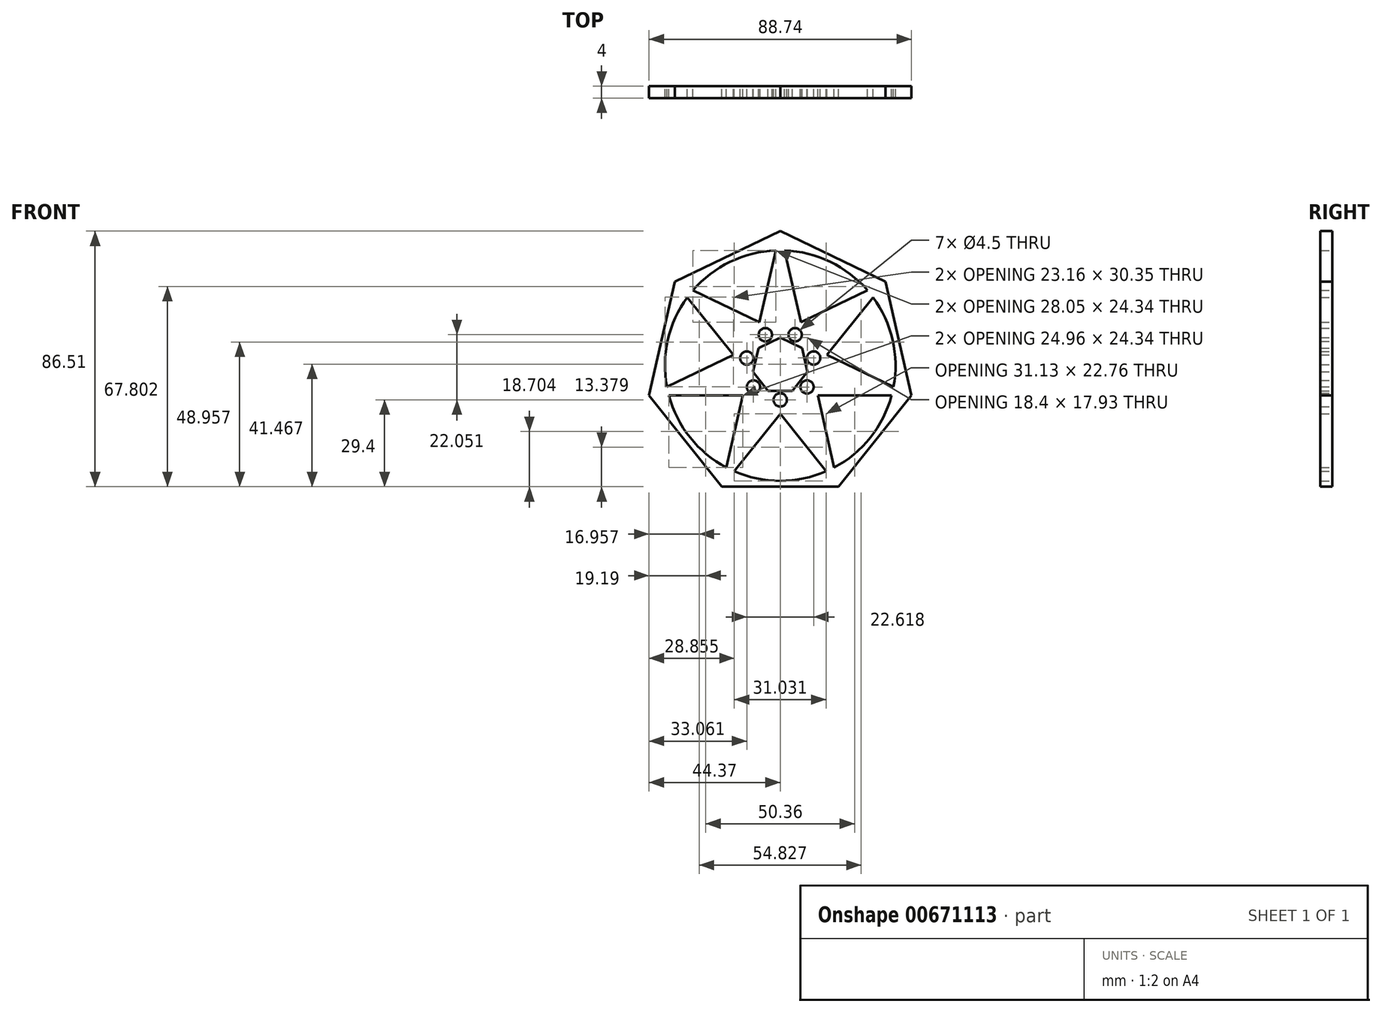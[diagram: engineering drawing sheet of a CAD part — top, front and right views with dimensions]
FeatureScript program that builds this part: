
annotation { "Feature Type Name" : "Feature", "Feature Type Description" : "" }
export const myFeature = defineFeature(function(context is Context, id is Id, definition is map)
    precondition{}
    {
        {
            var Q0;
            Q0=qCreatedBy(makeId("Front.planeOp"),FACE);
            var sketch = newSketch(context, id + "F0", { "sketchPlane" : qUnion([Q0])});
            skEllipse(sketch, "E0", {"center": v(0, 0) * mm, "majorRadius": 60 * mm, "minorRadius": 47.5 * mm, "majorAxis": v(-1, 0)});
            skLineSegment(sketch, "E1", {"start": v(-35.58, 28.37) * mm, "end": v(0, 11.24) * mm});
            skLineSegment(sketch, "E2", {"start": v(-35.58, 28.37) * mm, "end": v(-10.96, -2.5) * mm});
            skLineSegment(sketch, "E3", {"start": v(19.74, -41) * mm, "end": v(10.96, -2.5) * mm});
            skLineSegment(sketch, "E4", {"start": v(-19.74, -41) * mm, "end": v(4.88, -10.13) * mm});
            skLineSegment(sketch, "E5", {"start": v(-44.37, -10.13) * mm, "end": v(-4.88, -10.13) * mm});
            skLineSegment(sketch, "E6", {"start": v(0, 45.5) * mm, "end": v(-8.79, 7) * mm});
            skLineSegment(sketch, "E7", {"start": v(35.58, 28.37) * mm, "end": v(0, 11.24) * mm});
            skCircle(sketch, "E8.cCircle", {"center": v(0, 0) * mm, "radius": 8.5 * mm, "construction": true});
            skLineSegment(sketch, "E8.0", {"start": v(-7.38, 5.88) * mm, "end": v(0, 9.43) * mm});
            skLineSegment(sketch, "E8.1", {"start": v(0, 9.43) * mm, "end": v(7.38, 5.88) * mm});
            skLineSegment(sketch, "E8.2", {"start": v(7.38, 5.88) * mm, "end": v(9.2, -2.1) * mm});
            skLineSegment(sketch, "E8.3", {"start": v(9.2, -2.1) * mm, "end": v(4.1, -8.5) * mm});
            skLineSegment(sketch, "E8.4", {"start": v(4.1, -8.5) * mm, "end": v(-4.1, -8.5) * mm});
            skLineSegment(sketch, "E8.5", {"start": v(-4.1, -8.5) * mm, "end": v(-9.2, -2.1) * mm});
            skLineSegment(sketch, "E8.6", {"start": v(-9.2, -2.1) * mm, "end": v(-7.38, 5.88) * mm});
            skPoint(sketch, "E8.0.midPoint", {"position": v(-3.69, 7.66) * mm});
            skLineSegment(sketch, "E9.trimOffspring", {"start": v(-8.79, 7) * mm, "end": v(-44.37, -10.13) * mm});
            skLineSegment(sketch, "E10.trimOffspring", {"start": v(8.79, 7) * mm, "end": v(44.37, -10.13) * mm});
            skLineSegment(sketch, "E11.trimOffspring", {"start": v(8.79, 7) * mm, "end": v(0, 45.5) * mm});
            skLineSegment(sketch, "E12.trimOffspring", {"start": v(10.96, -2.5) * mm, "end": v(35.58, 28.37) * mm});
            skLineSegment(sketch, "E13.trimOffspring", {"start": v(4.88, -10.13) * mm, "end": v(44.37, -10.13) * mm});
            skLineSegment(sketch, "E14.trimOffspring", {"start": v(-4.88, -10.13) * mm, "end": v(19.74, -41) * mm});
            skLineSegment(sketch, "E15.trimOffspring", {"start": v(-10.96, -2.5) * mm, "end": v(-19.74, -41) * mm});
            skLineSegment(sketch, "E16", {"start": v(-15.83, 3.61) * mm, "end": v(0, 0) * mm, "construction": true});
            skCircle(sketch, "E17", {"center": v(-11.3, 2.58) * mm, "radius": 2.25 * mm});
            skCircle(sketch, "E18.1.0", {"center": v(-9.07, -7.23) * mm, "radius": 2.25 * mm});
            skCircle(sketch, "E18.2.0", {"center": v(0, -11.6) * mm, "radius": 2.25 * mm});
            skCircle(sketch, "E19.1.3.0", {"center": v(9.07, -7.23) * mm, "radius": 2.25 * mm});
            skCircle(sketch, "E19.1.4.0", {"center": v(11.3, 2.58) * mm, "radius": 2.25 * mm});
            skCircle(sketch, "E19.1.5.0", {"center": v(5.03, 10.45) * mm, "radius": 2.25 * mm});
            skCircle(sketch, "E19.1.6.0", {"center": v(-5.03, 10.45) * mm, "radius": 2.25 * mm});
            skCircle(sketch, "E20", {"center": v(0, 0) * mm, "radius": 39 * mm});
            skCircle(sketch, "E21.cCircle", {"center": v(0, 0) * mm, "radius": 41 * mm, "construction": true});
            skLineSegment(sketch, "E21.0", {"start": v(-35.58, 28.37) * mm, "end": v(0, 45.5) * mm});
            skLineSegment(sketch, "E21.1", {"start": v(0, 45.5) * mm, "end": v(35.58, 28.37) * mm});
            skLineSegment(sketch, "E21.2", {"start": v(35.58, 28.37) * mm, "end": v(44.37, -10.13) * mm});
            skLineSegment(sketch, "E21.3", {"start": v(44.37, -10.13) * mm, "end": v(19.74, -41) * mm});
            skLineSegment(sketch, "E21.4", {"start": v(19.74, -41) * mm, "end": v(-19.74, -41) * mm});
            skLineSegment(sketch, "E21.5", {"start": v(-19.74, -41) * mm, "end": v(-44.37, -10.13) * mm});
            skLineSegment(sketch, "E21.6", {"start": v(-44.37, -10.13) * mm, "end": v(-35.58, 28.37) * mm});
            skPoint(sketch, "E21.0.midPoint", {"position": v(-17.79, 36.94) * mm});
            skSolve(sketch);
        }
        {
            var Q0;
            {var subQ5=sQuery(id+"F0.wireOp",EDGE,"E1");var subQ7=sQuery(id+"F0.wireOp",EDGE,"E20");var subQ9=makeQuery(id+"F0.imprint","INTERSECT",VERTEX,{"derivedFrom":[subQ5,subQ7]});Q0=makeQuery(id+"F0.imprint","IMPRINT",FACE,{"disambiguationData":[TD([[makeQuery(id+"F0.imprint","IMPRINT",EDGE,{"disambiguationData":[TD([[subQ9,-1.0]])],"derivedFrom":subQ5}),-1.0]])]});}
            var Q1;
            {var subQ1=sQuery(id+"F0.wireOp",EDGE,"E7");var subQ5=sQuery(id+"F0.wireOp",EDGE,"E1");var subQ6=makeQuery(id+"F0.imprint","INTERSECT",VERTEX,{"derivedFrom":[subQ5,subQ1]});Q1=makeQuery(id+"F0.imprint","IMPRINT",FACE,{"disambiguationData":[TD([[makeQuery(id+"F0.imprint","IMPRINT",EDGE,{"disambiguationData":[TD([[subQ6,1.0]])],"derivedFrom":subQ5}),1.0]])]});}
            var Q2;
            Q2=makeQuery(id+"F0.imprint","IMPRINT",FACE,{"disambiguationData":[TD([[makeQuery(id+"F0.imprint","IMPRINT",EDGE,{"derivedFrom":sQuery(id+"F0.wireOp",EDGE,"E8.0")}),1.0]])]});
            var Q3;
            {var subQ3=sQuery(id+"F0.wireOp",EDGE,"E20");var subQ7=sQuery(id+"F0.wireOp",EDGE,"E7");var subQ9=makeQuery(id+"F0.imprint","INTERSECT",VERTEX,{"derivedFrom":[subQ7,subQ3]});Q3=makeQuery(id+"F0.imprint","IMPRINT",FACE,{"disambiguationData":[TD([[makeQuery(id+"F0.imprint","IMPRINT",EDGE,{"disambiguationData":[TD([[subQ9,-1.0]])],"derivedFrom":subQ7}),1.0]])]});}
            var Q4;
            {var subQ1=sQuery(id+"F0.wireOp",EDGE,"E3");var subQ5=sQuery(id+"F0.wireOp",EDGE,"E12.trimOffspring");var subQ6=makeQuery(id+"F0.imprint","INTERSECT",VERTEX,{"derivedFrom":[subQ1,subQ5]});Q4=makeQuery(id+"F0.imprint","IMPRINT",FACE,{"disambiguationData":[TD([[makeQuery(id+"F0.imprint","IMPRINT",EDGE,{"disambiguationData":[TD([[subQ6,1.0]])],"derivedFrom":subQ1}),-1.0]])]});}
            var Q5;
            {var subQ3=sQuery(id+"F0.wireOp",EDGE,"E20");var subQ7=sQuery(id+"F0.wireOp",EDGE,"E3");var subQ8=makeQuery(id+"F0.imprint","INTERSECT",VERTEX,{"derivedFrom":[subQ7,subQ3]});Q5=makeQuery(id+"F0.imprint","IMPRINT",FACE,{"disambiguationData":[TD([[makeQuery(id+"F0.imprint","IMPRINT",EDGE,{"disambiguationData":[TD([[subQ8,-1.0]])],"derivedFrom":subQ7}),1.0]])]});}
            var Q6;
            {var subQ3=sQuery(id+"F0.wireOp",EDGE,"E20");var subQ7=sQuery(id+"F0.wireOp",EDGE,"E4");var subQ9=makeQuery(id+"F0.imprint","INTERSECT",VERTEX,{"derivedFrom":[subQ7,subQ3]});Q6=makeQuery(id+"F0.imprint","IMPRINT",FACE,{"disambiguationData":[TD([[makeQuery(id+"F0.imprint","IMPRINT",EDGE,{"disambiguationData":[TD([[subQ9,-1.0]])],"derivedFrom":subQ7}),1.0]])]});}
            var Q7;
            {var subQ0=sQuery(id+"F0.wireOp",EDGE,"E15.trimOffspring");var subQ1=sQuery(id+"F0.wireOp",EDGE,"E2");var subQ2=makeQuery(id+"F0.imprint","INTERSECT",VERTEX,{"derivedFrom":[subQ1,subQ0]});Q7=makeQuery(id+"F0.imprint","IMPRINT",FACE,{"disambiguationData":[TD([[makeQuery(id+"F0.imprint","IMPRINT",EDGE,{"disambiguationData":[TD([[subQ2,1.0]])],"derivedFrom":subQ1}),-1.0]])]});}
            var Q8;
            {var subQ1=sQuery(id+"F0.wireOp",EDGE,"E1");var subQ3=sQuery(id+"F0.wireOp",EDGE,"E20");var subQ4=makeQuery(id+"F0.imprint","INTERSECT",VERTEX,{"derivedFrom":[subQ1,subQ3]});Q8=makeQuery(id+"F0.imprint","IMPRINT",FACE,{"disambiguationData":[TD([[makeQuery(id+"F0.imprint","IMPRINT",EDGE,{"disambiguationData":[TD([[subQ4,-1.0]])],"derivedFrom":subQ3}),-1.0]])]});}
            var Q9;
            {var subQ0=sQuery(id+"F0.wireOp",EDGE,"534f871a-39e5-4cf4-bd64-749bc5adb339.6");Q9=makeQuery(id+"F0.imprint","IMPRINT",FACE,{"disambiguationData":[TD([[makeQuery(id+"F0.imprint","IMPRINT",EDGE,{"derivedFrom":subQ0}),-1.0]])]});}
            var Q10;
            {var subQ0=sQuery(id+"F0.wireOp",EDGE,"534f871a-39e5-4cf4-bd64-749bc5adb339.5");Q10=makeQuery(id+"F0.imprint","IMPRINT",FACE,{"disambiguationData":[TD([[makeQuery(id+"F0.imprint","IMPRINT",EDGE,{"derivedFrom":subQ0}),-1.0]])]});}
            var Q11;
            {var subQ1=sQuery(id+"F0.wireOp",EDGE,"E6");var subQ3=sQuery(id+"F0.wireOp",EDGE,"E20");var subQ4=makeQuery(id+"F0.imprint","INTERSECT",VERTEX,{"derivedFrom":[subQ1,subQ3]});Q11=makeQuery(id+"F0.imprint","IMPRINT",FACE,{"disambiguationData":[TD([[makeQuery(id+"F0.imprint","IMPRINT",EDGE,{"disambiguationData":[TD([[subQ4,1.0]])],"derivedFrom":subQ3}),-1.0]])]});}
            var Q12;
            {var subQ0=sQuery(id+"F0.wireOp",EDGE,"534f871a-39e5-4cf4-bd64-749bc5adb339.0");Q12=makeQuery(id+"F0.imprint","IMPRINT",FACE,{"disambiguationData":[TD([[makeQuery(id+"F0.imprint","IMPRINT",EDGE,{"derivedFrom":subQ0}),-1.0]])]});}
            var Q13;
            {var subQ0=sQuery(id+"F0.wireOp",EDGE,"534f871a-39e5-4cf4-bd64-749bc5adb339.1");Q13=makeQuery(id+"F0.imprint","IMPRINT",FACE,{"disambiguationData":[TD([[makeQuery(id+"F0.imprint","IMPRINT",EDGE,{"derivedFrom":subQ0}),-1.0]])]});}
            var Q14;
            {var subQ0=sQuery(id+"F0.wireOp",EDGE,"534f871a-39e5-4cf4-bd64-749bc5adb339.1");Q14=makeQuery(id+"F0.imprint","IMPRINT",FACE,{"disambiguationData":[TD([[makeQuery(id+"F0.imprint","IMPRINT",EDGE,{"derivedFrom":subQ0}),1.0]])]});}
            var Q15;
            {var subQ0=sQuery(id+"F0.wireOp",EDGE,"534f871a-39e5-4cf4-bd64-749bc5adb339.0");Q15=makeQuery(id+"F0.imprint","IMPRINT",FACE,{"disambiguationData":[TD([[makeQuery(id+"F0.imprint","IMPRINT",EDGE,{"derivedFrom":subQ0}),1.0]])]});}
            var Q16;
            {var subQ0=sQuery(id+"F0.wireOp",EDGE,"534f871a-39e5-4cf4-bd64-749bc5adb339.6");Q16=makeQuery(id+"F0.imprint","IMPRINT",FACE,{"disambiguationData":[TD([[makeQuery(id+"F0.imprint","IMPRINT",EDGE,{"derivedFrom":subQ0}),1.0]])]});}
            var Q17;
            {var subQ0=sQuery(id+"F0.wireOp",EDGE,"534f871a-39e5-4cf4-bd64-749bc5adb339.5");Q17=makeQuery(id+"F0.imprint","IMPRINT",FACE,{"disambiguationData":[TD([[makeQuery(id+"F0.imprint","IMPRINT",EDGE,{"derivedFrom":subQ0}),1.0]])]});}
            var Q18;
            {var subQ0=sQuery(id+"F0.wireOp",EDGE,"534f871a-39e5-4cf4-bd64-749bc5adb339.4");Q18=makeQuery(id+"F0.imprint","IMPRINT",FACE,{"disambiguationData":[TD([[makeQuery(id+"F0.imprint","IMPRINT",EDGE,{"derivedFrom":subQ0}),-1.0]])]});}
            var Q19;
            {var subQ1=sQuery(id+"F0.wireOp",EDGE,"E5");var subQ3=sQuery(id+"F0.wireOp",EDGE,"E20");var subQ4=makeQuery(id+"F0.imprint","INTERSECT",VERTEX,{"derivedFrom":[subQ1,subQ3]});Q19=makeQuery(id+"F0.imprint","IMPRINT",FACE,{"disambiguationData":[TD([[makeQuery(id+"F0.imprint","IMPRINT",EDGE,{"disambiguationData":[TD([[subQ4,1.0]])],"derivedFrom":subQ3}),-1.0]])]});}
            var Q20;
            {var subQ0=sQuery(id+"F0.wireOp",EDGE,"534f871a-39e5-4cf4-bd64-749bc5adb339.4");Q20=makeQuery(id+"F0.imprint","IMPRINT",FACE,{"disambiguationData":[TD([[makeQuery(id+"F0.imprint","IMPRINT",EDGE,{"derivedFrom":subQ0}),1.0]])]});}
            var Q21;
            {var subQ1=sQuery(id+"F0.wireOp",EDGE,"E7");var subQ3=sQuery(id+"F0.wireOp",EDGE,"E20");var subQ4=makeQuery(id+"F0.imprint","INTERSECT",VERTEX,{"derivedFrom":[subQ1,subQ3]});Q21=makeQuery(id+"F0.imprint","IMPRINT",FACE,{"disambiguationData":[TD([[makeQuery(id+"F0.imprint","IMPRINT",EDGE,{"disambiguationData":[TD([[subQ4,1.0]])],"derivedFrom":subQ3}),-1.0]])]});}
            var Q22;
            {var subQ1=sQuery(id+"F0.wireOp",EDGE,"E10.trimOffspring");var subQ3=sQuery(id+"F0.wireOp",EDGE,"E20");var subQ4=makeQuery(id+"F0.imprint","INTERSECT",VERTEX,{"derivedFrom":[subQ1,subQ3]});Q22=makeQuery(id+"F0.imprint","IMPRINT",FACE,{"disambiguationData":[TD([[makeQuery(id+"F0.imprint","IMPRINT",EDGE,{"disambiguationData":[TD([[subQ4,1.0]])],"derivedFrom":subQ3}),-1.0]])]});}
            var Q23;
            {var subQ0=sQuery(id+"F0.wireOp",EDGE,"534f871a-39e5-4cf4-bd64-749bc5adb339.2");Q23=makeQuery(id+"F0.imprint","IMPRINT",FACE,{"disambiguationData":[TD([[makeQuery(id+"F0.imprint","IMPRINT",EDGE,{"derivedFrom":subQ0}),-1.0]])]});}
            var Q24;
            {var subQ0=sQuery(id+"F0.wireOp",EDGE,"534f871a-39e5-4cf4-bd64-749bc5adb339.2");Q24=makeQuery(id+"F0.imprint","IMPRINT",FACE,{"disambiguationData":[TD([[makeQuery(id+"F0.imprint","IMPRINT",EDGE,{"derivedFrom":subQ0}),1.0]])]});}
            var Q25;
            {var subQ0=sQuery(id+"F0.wireOp",EDGE,"534f871a-39e5-4cf4-bd64-749bc5adb339.3");Q25=makeQuery(id+"F0.imprint","IMPRINT",FACE,{"disambiguationData":[TD([[makeQuery(id+"F0.imprint","IMPRINT",EDGE,{"derivedFrom":subQ0}),1.0]])]});}
            var Q26;
            {var subQ0=sQuery(id+"F0.wireOp",EDGE,"534f871a-39e5-4cf4-bd64-749bc5adb339.3");Q26=makeQuery(id+"F0.imprint","IMPRINT",FACE,{"disambiguationData":[TD([[makeQuery(id+"F0.imprint","IMPRINT",EDGE,{"derivedFrom":subQ0}),-1.0]])]});}
            var Q27;
            {var subQ1=sQuery(id+"F0.wireOp",EDGE,"E3");var subQ3=sQuery(id+"F0.wireOp",EDGE,"E20");var subQ4=makeQuery(id+"F0.imprint","INTERSECT",VERTEX,{"derivedFrom":[subQ1,subQ3]});Q27=makeQuery(id+"F0.imprint","IMPRINT",FACE,{"disambiguationData":[TD([[makeQuery(id+"F0.imprint","IMPRINT",EDGE,{"disambiguationData":[TD([[subQ4,1.0]])],"derivedFrom":subQ3}),-1.0]])]});}
            var Q28;
            {var subQ1=sQuery(id+"F0.wireOp",EDGE,"E4");var subQ3=sQuery(id+"F0.wireOp",EDGE,"E20");var subQ4=makeQuery(id+"F0.imprint","INTERSECT",VERTEX,{"derivedFrom":[subQ1,subQ3]});Q28=makeQuery(id+"F0.imprint","IMPRINT",FACE,{"disambiguationData":[TD([[makeQuery(id+"F0.imprint","IMPRINT",EDGE,{"disambiguationData":[TD([[subQ4,1.0]])],"derivedFrom":subQ3}),-1.0]])]});}
            var Q29;
            {var subQ0=sQuery(id+"F0.wireOp",EDGE,"E21.0");Q29=makeQuery(id+"F0.imprint","IMPRINT",FACE,{"disambiguationData":[TD([[makeQuery(id+"F0.imprint","IMPRINT",EDGE,{"derivedFrom":subQ0}),-1.0]])]});}
            var Q30;
            {var subQ0=sQuery(id+"F0.wireOp",EDGE,"E21.6");Q30=makeQuery(id+"F0.imprint","IMPRINT",FACE,{"disambiguationData":[TD([[makeQuery(id+"F0.imprint","IMPRINT",EDGE,{"derivedFrom":subQ0}),-1.0]])]});}
            var Q31;
            {var subQ0=sQuery(id+"F0.wireOp",EDGE,"E21.1");Q31=makeQuery(id+"F0.imprint","IMPRINT",FACE,{"disambiguationData":[TD([[makeQuery(id+"F0.imprint","IMPRINT",EDGE,{"derivedFrom":subQ0}),-1.0]])]});}
            var Q32;
            {var subQ0=sQuery(id+"F0.wireOp",EDGE,"E21.2");Q32=makeQuery(id+"F0.imprint","IMPRINT",FACE,{"disambiguationData":[TD([[makeQuery(id+"F0.imprint","IMPRINT",EDGE,{"derivedFrom":subQ0}),-1.0]])]});}
            var Q33;
            {var subQ0=sQuery(id+"F0.wireOp",EDGE,"E21.3");Q33=makeQuery(id+"F0.imprint","IMPRINT",FACE,{"disambiguationData":[TD([[makeQuery(id+"F0.imprint","IMPRINT",EDGE,{"derivedFrom":subQ0}),-1.0]])]});}
            var Q34;
            {var subQ0=sQuery(id+"F0.wireOp",EDGE,"E21.4");Q34=makeQuery(id+"F0.imprint","IMPRINT",FACE,{"disambiguationData":[TD([[makeQuery(id+"F0.imprint","IMPRINT",EDGE,{"derivedFrom":subQ0}),-1.0]])]});}
            var Q35;
            {var subQ0=sQuery(id+"F0.wireOp",EDGE,"E21.5");Q35=makeQuery(id+"F0.imprint","IMPRINT",FACE,{"disambiguationData":[TD([[makeQuery(id+"F0.imprint","IMPRINT",EDGE,{"derivedFrom":subQ0}),-1.0]])]});}
            extrude(context, id + "F1", {"entities" : qUnion([Q0, Q1, Q2, Q3, Q4, Q5, Q6, Q7, Q8, Q9, Q10, Q11, Q12, Q13, Q14, Q15, Q16, Q17, Q18, Q19, Q20, Q21, Q22, Q23, Q24, Q25, Q26, Q27, Q28, Q29, Q30, Q31, Q32, Q33, Q34, Q35]), "depth" : 4 * mm, "offsetDistance" : 25 * mm});
        }
    });
